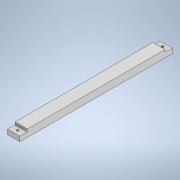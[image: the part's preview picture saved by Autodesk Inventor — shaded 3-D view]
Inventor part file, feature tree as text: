
AUTODESK INVENTOR PART (.ipt)
format: ipt  version: 2020 (Build 240168000, 168)  size: 123,392 bytes
history: native  units: mm
features: sketch x2, other x1, extrude x1, hole x1, projected_geometry x1
ambient origin geometry x8: Origin, YZ Plane, XZ Plane, XY Plane, X Axis, Y Axis, Z Axis, Center Point
bodies: Body1 (feature_tree)
feature tree (6):
  other  "솔리드1"
  extrude  "돌출1"  Depth=308.857mm
  hole  "구멍3"  [1 undecoded]
  sketch  "스케치1"
  sketch  "스케치3"
  projected_geometry  "투영된 루프1"
note: 1 required parameter value undecoded (feature->parameter linkage not recoverable at this tier; creation-order binding heuristic only, values carry confidence <= 0.55)
